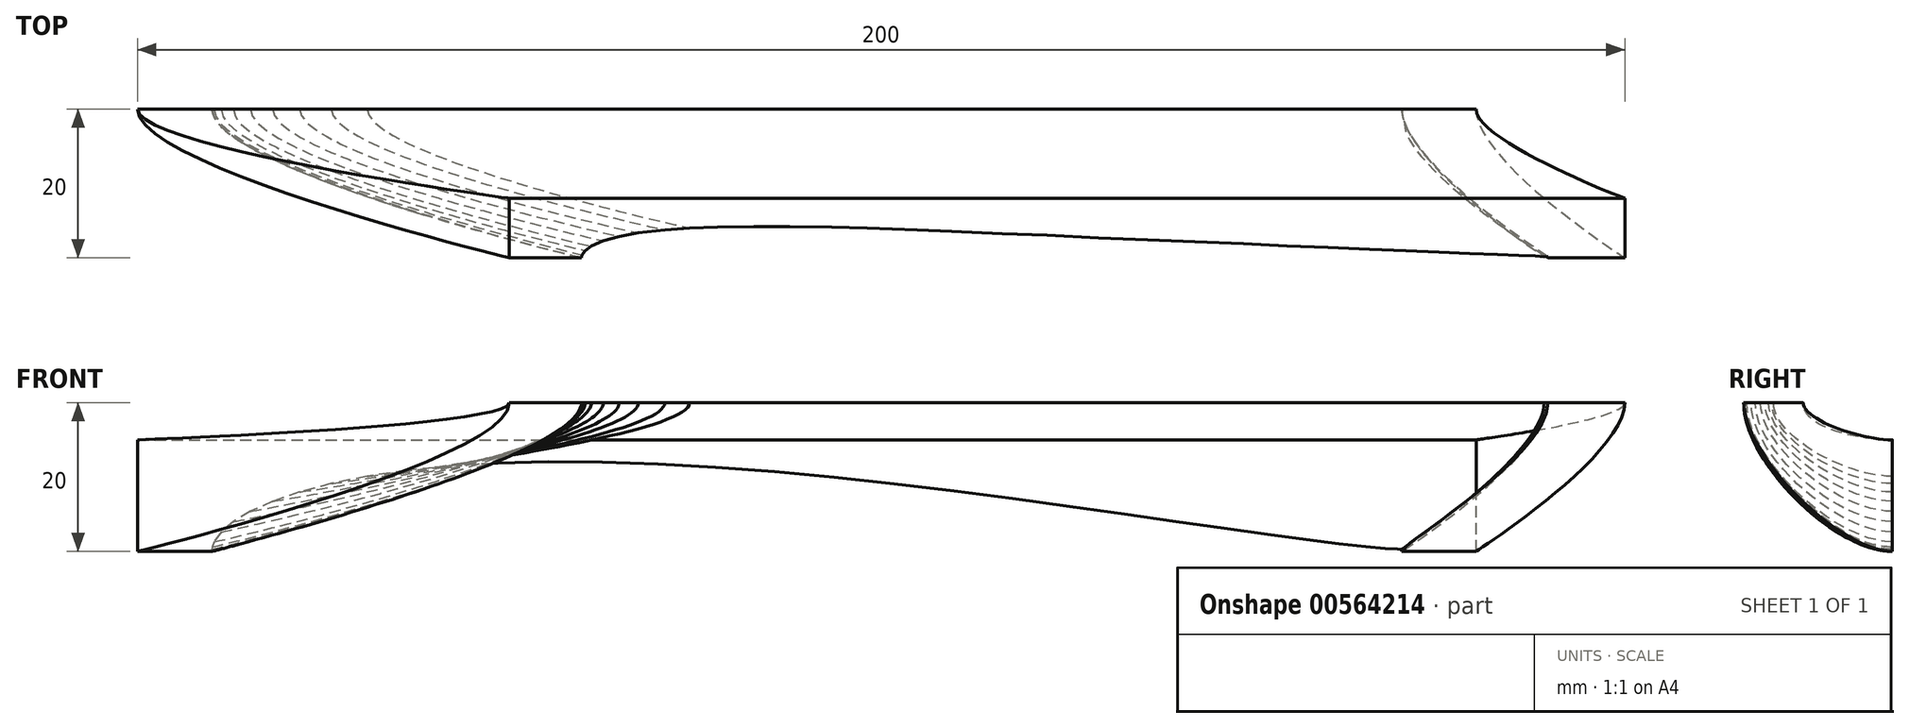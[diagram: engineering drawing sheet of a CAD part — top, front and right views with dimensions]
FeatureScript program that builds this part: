
annotation { "Feature Type Name" : "Feature", "Feature Type Description" : "" }
export const myFeature = defineFeature(function(context is Context, id is Id, definition is map)
    precondition{}
    {
        {
            var Q0;
            Q0=qCreatedBy(makeId("Top.planeOp"),FACE);
            cPlane(context, id + "F0", {"entities" : qUnion([Q0]), "cplaneType" : CPlaneType.OFFSET, "offset" : 20 * mm, "width" : 150 * mm, "height" : 150 * mm});
        }
        {
            var Q0;
            Q0=qCreatedBy(id+"F0.planeOp",FACE);
            var sketch = newSketch(context, id + "F1", { "sketchPlane" : qUnion([Q0])});
            skLineSegment(sketch, "E0", {"start": v(19.7, -19.84) * mm, "end": v(19.16, -19.85) * mm});
            skLineSegment(sketch, "E1", {"start": v(19.16, -19.85) * mm, "end": v(17.98, -19.78) * mm});
            skLineSegment(sketch, "E2", {"start": v(17.98, -19.78) * mm, "end": v(15.76, -19.7) * mm});
            skLineSegment(sketch, "E3", {"start": v(15.76, -19.7) * mm, "end": v(12.9, -19.56) * mm});
            skLineSegment(sketch, "E4", {"start": v(12.9, -19.56) * mm, "end": v(9.15, -19.4) * mm});
            skLineSegment(sketch, "E5", {"start": v(9.15, -19.4) * mm, "end": v(5.03, -19.25) * mm});
            skLineSegment(sketch, "E6", {"start": v(5.03, -19.25) * mm, "end": v(0.59, -19.04) * mm});
            skLineSegment(sketch, "E7", {"start": v(0.59, -19.04) * mm, "end": v(-4.3, -18.86) * mm});
            skLineSegment(sketch, "E8", {"start": v(-4.3, -18.86) * mm, "end": v(-9.93, -18.58) * mm});
            skLineSegment(sketch, "E9", {"start": v(-9.93, -18.58) * mm, "end": v(-15.46, -18.4) * mm});
            skLineSegment(sketch, "E10", {"start": v(-15.46, -18.4) * mm, "end": v(-21.25, -18.11) * mm});
            skLineSegment(sketch, "E11", {"start": v(-21.25, -18.11) * mm, "end": v(-27.83, -17.85) * mm});
            skLineSegment(sketch, "E12", {"start": v(-27.83, -17.85) * mm, "end": v(-34.17, -17.6) * mm});
            skLineSegment(sketch, "E13", {"start": v(-34.17, -17.6) * mm, "end": v(-40.77, -17.32) * mm});
            skLineSegment(sketch, "E14", {"start": v(-40.77, -17.32) * mm, "end": v(-47.7, -16.97) * mm});
            skLineSegment(sketch, "E15", {"start": v(-47.7, -16.97) * mm, "end": v(-53.75, -16.74) * mm});
            skLineSegment(sketch, "E16", {"start": v(-53.75, -16.74) * mm, "end": v(-60.52, -16.43) * mm});
            skLineSegment(sketch, "E17", {"start": v(-60.52, -16.43) * mm, "end": v(-65.14, -16.26) * mm});
            skLineSegment(sketch, "E18", {"start": v(-65.14, -16.26) * mm, "end": v(-71.91, -16.02) * mm});
            skLineSegment(sketch, "E19", {"start": v(-71.91, -16.02) * mm, "end": v(-76.64, -15.9) * mm});
            skLineSegment(sketch, "E20", {"start": v(-76.64, -15.9) * mm, "end": v(-82.29, -15.8) * mm});
            skLineSegment(sketch, "E21", {"start": v(-82.29, -15.8) * mm, "end": v(-87.14, -15.78) * mm});
            skLineSegment(sketch, "E22", {"start": v(-87.14, -15.78) * mm, "end": v(-92, -15.85) * mm});
            skLineSegment(sketch, "E23", {"start": v(-92, -15.85) * mm, "end": v(-95.73, -16) * mm});
            skLineSegment(sketch, "E24", {"start": v(-95.73, -16) * mm, "end": v(-99.09, -16.25) * mm});
            skLineSegment(sketch, "E25", {"start": v(-99.09, -16.25) * mm, "end": v(-102.67, -16.66) * mm});
            skLineSegment(sketch, "E26", {"start": v(-102.67, -16.66) * mm, "end": v(-105.25, -17.11) * mm});
            skLineSegment(sketch, "E27", {"start": v(-105.25, -17.11) * mm, "end": v(-107.38, -17.72) * mm});
            skLineSegment(sketch, "E28", {"start": v(-107.38, -17.72) * mm, "end": v(-108.98, -18.44) * mm});
            skLineSegment(sketch, "E29", {"start": v(-108.98, -18.44) * mm, "end": v(-109.81, -19.02) * mm});
            skLineSegment(sketch, "E30", {"start": v(-109.81, -19.02) * mm, "end": v(-110.22, -19.6) * mm});
            skLineSegment(sketch, "E31", {"start": v(-110.22, -19.6) * mm, "end": v(-110.3, -20) * mm});
            skLineSegment(sketch, "E32", {"start": v(-110.3, -20) * mm, "end": v(-110.27, -20.22) * mm});
            skLineSegment(sketch, "E33", {"start": v(-110.27, -20.22) * mm, "end": v(-110.22, -20.45) * mm});
            skLineSegment(sketch, "E34", {"start": v(-110.22, -20.45) * mm, "end": v(-110.08, -20.67) * mm});
            skLineSegment(sketch, "E35", {"start": v(-110.08, -20.67) * mm, "end": v(-109.3, -21.38) * mm});
            skLineSegment(sketch, "E36", {"start": v(-109.3, -21.38) * mm, "end": v(-108.23, -21.93) * mm});
            skLineSegment(sketch, "E37", {"start": v(-108.23, -21.93) * mm, "end": v(-106.57, -22.53) * mm});
            skLineSegment(sketch, "E38", {"start": v(-106.57, -22.53) * mm, "end": v(-103.96, -23.13) * mm});
            skLineSegment(sketch, "E39", {"start": v(-103.96, -23.13) * mm, "end": v(-100.94, -23.57) * mm});
            skLineSegment(sketch, "E40", {"start": v(-100.94, -23.57) * mm, "end": v(-97.12, -23.91) * mm});
            skLineSegment(sketch, "E41", {"start": v(-97.12, -23.91) * mm, "end": v(-92.73, -24.14) * mm});
            skLineSegment(sketch, "E42", {"start": v(-92.73, -24.14) * mm, "end": v(-87.63, -24.2) * mm});
            skLineSegment(sketch, "E43", {"start": v(-87.63, -24.2) * mm, "end": v(-82.12, -24.22) * mm});
            skLineSegment(sketch, "E44", {"start": v(-82.12, -24.22) * mm, "end": v(-76.28, -24.06) * mm});
            skLineSegment(sketch, "E45", {"start": v(-76.28, -24.06) * mm, "end": v(-70.12, -23.88) * mm});
            skLineSegment(sketch, "E46", {"start": v(-70.12, -23.88) * mm, "end": v(-63.57, -23.67) * mm});
            skLineSegment(sketch, "E47", {"start": v(-63.57, -23.67) * mm, "end": v(-56.78, -23.4) * mm});
            skLineSegment(sketch, "E48", {"start": v(-56.78, -23.4) * mm, "end": v(-49.1, -23.04) * mm});
            skLineSegment(sketch, "E49", {"start": v(-49.1, -23.04) * mm, "end": v(-42.6, -22.76) * mm});
            skLineSegment(sketch, "E50", {"start": v(-42.6, -22.76) * mm, "end": v(-36.05, -22.49) * mm});
            skLineSegment(sketch, "E51", {"start": v(-36.05, -22.49) * mm, "end": v(-28.85, -22.17) * mm});
            skLineSegment(sketch, "E52", {"start": v(-28.85, -22.17) * mm, "end": v(-22.14, -21.9) * mm});
            skLineSegment(sketch, "E53", {"start": v(-22.14, -21.9) * mm, "end": v(-15.69, -21.62) * mm});
            skLineSegment(sketch, "E54", {"start": v(-15.69, -21.62) * mm, "end": v(-9.54, -21.37) * mm});
            skLineSegment(sketch, "E55", {"start": v(-9.54, -21.37) * mm, "end": v(-3.88, -21.13) * mm});
            skLineSegment(sketch, "E56", {"start": v(-3.88, -21.13) * mm, "end": v(1.4, -20.9) * mm});
            skLineSegment(sketch, "E57", {"start": v(1.4, -20.9) * mm, "end": v(5.8, -20.72) * mm});
            skLineSegment(sketch, "E58", {"start": v(5.8, -20.72) * mm, "end": v(9.8, -20.54) * mm});
            skLineSegment(sketch, "E59", {"start": v(9.8, -20.54) * mm, "end": v(13.11, -20.43) * mm});
            skLineSegment(sketch, "E60", {"start": v(13.11, -20.43) * mm, "end": v(15.93, -20.29) * mm});
            skLineSegment(sketch, "E61", {"start": v(15.93, -20.29) * mm, "end": v(17.9, -20.2) * mm});
            skLineSegment(sketch, "E62", {"start": v(17.9, -20.2) * mm, "end": v(19.7, -20.13) * mm});
            skLineSegment(sketch, "E63", {"start": v(19.7, -20.13) * mm, "end": v(19.7, -19.84) * mm});
            skSolve(sketch);
        }
        {
            var Q0;
            Q0=qCreatedBy(makeId("Front.planeOp"),FACE);
            var sketch = newSketch(context, id + "F2", { "sketchPlane" : qUnion([Q0])});
            skLineSegment(sketch, "E64", {"start": v(0, 0.27) * mm, "end": v(-0.56, 0.3) * mm});
            skLineSegment(sketch, "E65", {"start": v(-0.56, 0.3) * mm, "end": v(-2.2, 0.4) * mm});
            skLineSegment(sketch, "E66", {"start": v(-2.2, 0.4) * mm, "end": v(-4.85, 0.64) * mm});
            skLineSegment(sketch, "E67", {"start": v(-4.85, 0.64) * mm, "end": v(-8.43, 1.04) * mm});
            skLineSegment(sketch, "E68", {"start": v(-8.43, 1.04) * mm, "end": v(-12.86, 1.6) * mm});
            skLineSegment(sketch, "E69", {"start": v(-12.86, 1.6) * mm, "end": v(-18.04, 2.29) * mm});
            skLineSegment(sketch, "E70", {"start": v(-18.04, 2.29) * mm, "end": v(-23.9, 3.1) * mm});
            skLineSegment(sketch, "E71", {"start": v(-23.9, 3.1) * mm, "end": v(-30.35, 4.03) * mm});
            skLineSegment(sketch, "E72", {"start": v(-30.35, 4.03) * mm, "end": v(-37.3, 5.02) * mm});
            skLineSegment(sketch, "E73", {"start": v(-37.3, 5.02) * mm, "end": v(-44.65, 6.06) * mm});
            skLineSegment(sketch, "E74", {"start": v(-44.65, 6.06) * mm, "end": v(-52.32, 7.1) * mm});
            skLineSegment(sketch, "E75", {"start": v(-52.32, 7.1) * mm, "end": v(-60.2, 8.12) * mm});
            skLineSegment(sketch, "E76", {"start": v(-60.2, 8.12) * mm, "end": v(-68.23, 9.09) * mm});
            skLineSegment(sketch, "E77", {"start": v(-68.23, 9.09) * mm, "end": v(-76.31, 9.96) * mm});
            skLineSegment(sketch, "E78", {"start": v(-76.31, 9.96) * mm, "end": v(-84.36, 10.71) * mm});
            skLineSegment(sketch, "E79", {"start": v(-84.36, 10.71) * mm, "end": v(-92.3, 11.32) * mm});
            skLineSegment(sketch, "E80", {"start": v(-92.3, 11.32) * mm, "end": v(-100.04, 11.75) * mm});
            skLineSegment(sketch, "E81", {"start": v(-100.04, 11.75) * mm, "end": v(-107.54, 12) * mm});
            skLineSegment(sketch, "E82", {"start": v(-107.54, 12) * mm, "end": v(-114.72, 12.04) * mm});
            skLineSegment(sketch, "E83", {"start": v(-114.72, 12.04) * mm, "end": v(-121.52, 11.88) * mm});
            skLineSegment(sketch, "E84", {"start": v(-121.52, 11.88) * mm, "end": v(-127.88, 11.5) * mm});
            skLineSegment(sketch, "E85", {"start": v(-127.88, 11.5) * mm, "end": v(-133.77, 10.9) * mm});
            skLineSegment(sketch, "E86", {"start": v(-133.77, 10.9) * mm, "end": v(-139.14, 10.1) * mm});
            skLineSegment(sketch, "E87", {"start": v(-139.14, 10.1) * mm, "end": v(-143.97, 9.12) * mm});
            skLineSegment(sketch, "E88", {"start": v(-143.97, 9.12) * mm, "end": v(-148.2, 7.98) * mm});
            skLineSegment(sketch, "E89", {"start": v(-148.2, 7.98) * mm, "end": v(-151.82, 6.73) * mm});
            skLineSegment(sketch, "E90", {"start": v(-151.82, 6.73) * mm, "end": v(-154.8, 5.38) * mm});
            skLineSegment(sketch, "E91", {"start": v(-154.8, 5.38) * mm, "end": v(-157.13, 4) * mm});
            skLineSegment(sketch, "E92", {"start": v(-157.13, 4) * mm, "end": v(-158.77, 2.6) * mm});
            skLineSegment(sketch, "E93", {"start": v(-158.77, 2.6) * mm, "end": v(-159.73, 1.27) * mm});
            skLineSegment(sketch, "E94", {"start": v(-159.73, 1.27) * mm, "end": v(-159.97, 0.57) * mm});
            skLineSegment(sketch, "E95", {"start": v(-159.97, 0.57) * mm, "end": v(-160, 0.3) * mm});
            skLineSegment(sketch, "E96", {"start": v(-160, 0.3) * mm, "end": v(-159.98, 0.04) * mm});
            skLineSegment(sketch, "E97", {"start": v(-159.98, 0.04) * mm, "end": v(-159.89, -0.2) * mm});
            skLineSegment(sketch, "E98", {"start": v(-159.89, -0.2) * mm, "end": v(-159.73, -0.44) * mm});
            skLineSegment(sketch, "E99", {"start": v(-159.73, -0.44) * mm, "end": v(-159.34, -0.86) * mm});
            skLineSegment(sketch, "E100", {"start": v(-159.34, -0.86) * mm, "end": v(-157.85, -1.76) * mm});
            skLineSegment(sketch, "E101", {"start": v(-157.85, -1.76) * mm, "end": v(-155.56, -2.55) * mm});
            skLineSegment(sketch, "E102", {"start": v(-155.56, -2.55) * mm, "end": v(-152.48, -3.18) * mm});
            skLineSegment(sketch, "E103", {"start": v(-152.48, -3.18) * mm, "end": v(-148.6, -3.65) * mm});
            skLineSegment(sketch, "E104", {"start": v(-148.6, -3.65) * mm, "end": v(-143.95, -3.96) * mm});
            skLineSegment(sketch, "E105", {"start": v(-143.95, -3.96) * mm, "end": v(-138.56, -4.14) * mm});
            skLineSegment(sketch, "E106", {"start": v(-138.56, -4.14) * mm, "end": v(-132.48, -4.2) * mm});
            skLineSegment(sketch, "E107", {"start": v(-132.48, -4.2) * mm, "end": v(-125.76, -4.16) * mm});
            skLineSegment(sketch, "E108", {"start": v(-125.76, -4.16) * mm, "end": v(-118.5, -4.04) * mm});
            skLineSegment(sketch, "E109", {"start": v(-118.5, -4.04) * mm, "end": v(-110.75, -3.85) * mm});
            skLineSegment(sketch, "E110", {"start": v(-110.75, -3.85) * mm, "end": v(-102.62, -3.61) * mm});
            skLineSegment(sketch, "E111", {"start": v(-102.62, -3.61) * mm, "end": v(-94.21, -3.34) * mm});
            skLineSegment(sketch, "E112", {"start": v(-94.21, -3.34) * mm, "end": v(-85.61, -3.05) * mm});
            skLineSegment(sketch, "E113", {"start": v(-85.61, -3.05) * mm, "end": v(-76.93, -2.74) * mm});
            skLineSegment(sketch, "E114", {"start": v(-76.93, -2.74) * mm, "end": v(-68.27, -2.44) * mm});
            skLineSegment(sketch, "E115", {"start": v(-68.27, -2.44) * mm, "end": v(-59.74, -2.14) * mm});
            skLineSegment(sketch, "E116", {"start": v(-59.74, -2.14) * mm, "end": v(-51.45, -1.85) * mm});
            skLineSegment(sketch, "E117", {"start": v(-51.45, -1.85) * mm, "end": v(-43.49, -1.58) * mm});
            skLineSegment(sketch, "E118", {"start": v(-43.49, -1.58) * mm, "end": v(-35.95, -1.32) * mm});
            skLineSegment(sketch, "E119", {"start": v(-35.95, -1.32) * mm, "end": v(-28.94, -1.08) * mm});
            skLineSegment(sketch, "E120", {"start": v(-28.94, -1.08) * mm, "end": v(-22.53, -0.87) * mm});
            skLineSegment(sketch, "E121", {"start": v(-22.53, -0.87) * mm, "end": v(-16.82, -0.67) * mm});
            skLineSegment(sketch, "E122", {"start": v(-16.82, -0.67) * mm, "end": v(-11.85, -0.48) * mm});
            skLineSegment(sketch, "E123", {"start": v(-11.85, -0.48) * mm, "end": v(-7.7, -0.3) * mm});
            skLineSegment(sketch, "E124", {"start": v(-7.7, -0.3) * mm, "end": v(-4.43, -0.13) * mm});
            skLineSegment(sketch, "E125", {"start": v(-4.43, -0.13) * mm, "end": v(-1.86, -0.02) * mm});
            skLineSegment(sketch, "E126", {"start": v(-1.86, -0.02) * mm, "end": v(0, 0) * mm});
            skLineSegment(sketch, "E127", {"start": v(0, 0) * mm, "end": v(0, 0.27) * mm});
            skSolve(sketch);
        }
        {
            var Q0;
            Q0=qSketchRegion(id+"F2",true);
            var Q1;
            Q1=qSketchRegion(id+"F1",true);
            loft(context, id + "F3", {"startCondition" : LoftEndDerivativeType.NORMAL_TO_PROFILE, "startMagnitude" : 1, "endCondition" : LoftEndDerivativeType.NORMAL_TO_PROFILE, "endMagnitude" : 1, "sheetProfilesArray" : [{ "sheetProfileEntities" : qUnion([Q0]) }, { "sheetProfileEntities" : qUnion([Q1]) }]});
        }
        {
            var Q0;
            Q0=qCreatedBy(makeId("Front.planeOp"),FACE);
            var sketch = newSketch(context, id + "F4", { "sketchPlane" : qUnion([Q0])});
            skLineSegment(sketch, "E128.bottom", {"start": v(-170, 0) * mm, "end": v(10, 0) * mm});
            skLineSegment(sketch, "E128.top", {"start": v(-170, 15) * mm, "end": v(10, 15) * mm});
            skLineSegment(sketch, "E128.left", {"start": v(-170, 0) * mm, "end": v(-170, 15) * mm});
            skLineSegment(sketch, "E128.right", {"start": v(10, 0) * mm, "end": v(10, 15) * mm});
            skSolve(sketch);
        }
        {
            var Q0;
            Q0=qCreatedBy(id+"F0.planeOp",FACE);
            var sketch = newSketch(context, id + "F5", { "sketchPlane" : qUnion([Q0])});
            skLineSegment(sketch, "E129.bottom", {"start": v(-120, -20) * mm, "end": v(30, -20) * mm});
            skLineSegment(sketch, "E129.top", {"start": v(-120, -12) * mm, "end": v(30, -12) * mm});
            skLineSegment(sketch, "E129.left", {"start": v(-120, -20) * mm, "end": v(-120, -12) * mm});
            skLineSegment(sketch, "E129.right", {"start": v(30, -20) * mm, "end": v(30, -12) * mm});
            skSolve(sketch);
        }
        {
            var Q1;
            Q1 = qSketchRegion(id + "F4", true);
            var Q2;
            Q2 = qSketchRegion(id + "F5", true);
            loft(context, id + "F6", {"startCondition" : LoftEndDerivativeType.NORMAL_TO_PROFILE, "startMagnitude" : 1, "endCondition" : LoftEndDerivativeType.NORMAL_TO_PROFILE, "endMagnitude" : 1, "sheetProfilesArray" : [{ "sheetProfileEntities" : qUnion([Q1]) }, { "sheetProfileEntities" : qUnion([Q2]) }]});
        }
        {
            var Q0;
            Q0=makeQuery(id+"F3.opLoft","SWEPT_BODY",BODY,{"disambiguationData":[OSD([makeQuery(id+"F1.imprint","IMPRINT",FACE,{"disambiguationData":[TD([[makeQuery(id+"F1.imprint","IMPRINT",EDGE,{"derivedFrom":sQuery(id+"F1.wireOp",EDGE,"E0")}),1.0]])]}),makeQuery(id+"F2.imprint","IMPRINT",FACE,{"disambiguationData":[TD([[makeQuery(id+"F2.imprint","IMPRINT",EDGE,{"derivedFrom":sQuery(id+"F2.wireOp",EDGE,"E64")}),1.0]])]})])]});
            var Q1;
            Q1=makeQuery(id+"F6.opLoft","SWEPT_BODY",BODY,{"disambiguationData":[OSD([makeQuery(id+"F4.imprint","IMPRINT",FACE,{"disambiguationData":[TD([[makeQuery(id+"F4.imprint","IMPRINT",EDGE,{"derivedFrom":sQuery(id+"F4.wireOp",EDGE,"E128.bottom")}),1.0]])]}),makeQuery(id+"F5.imprint","IMPRINT",FACE,{"disambiguationData":[TD([[makeQuery(id+"F5.imprint","IMPRINT",EDGE,{"derivedFrom":sQuery(id+"F5.wireOp",EDGE,"E129.bottom")}),1.0]])]})])]});
            booleanBodies(context, id + "F7", {"operationType" : BooleanOperationType.SUBTRACTION, "tools" : qUnion([Q0]), "targets" : qUnion([Q1])});
        }
    });
